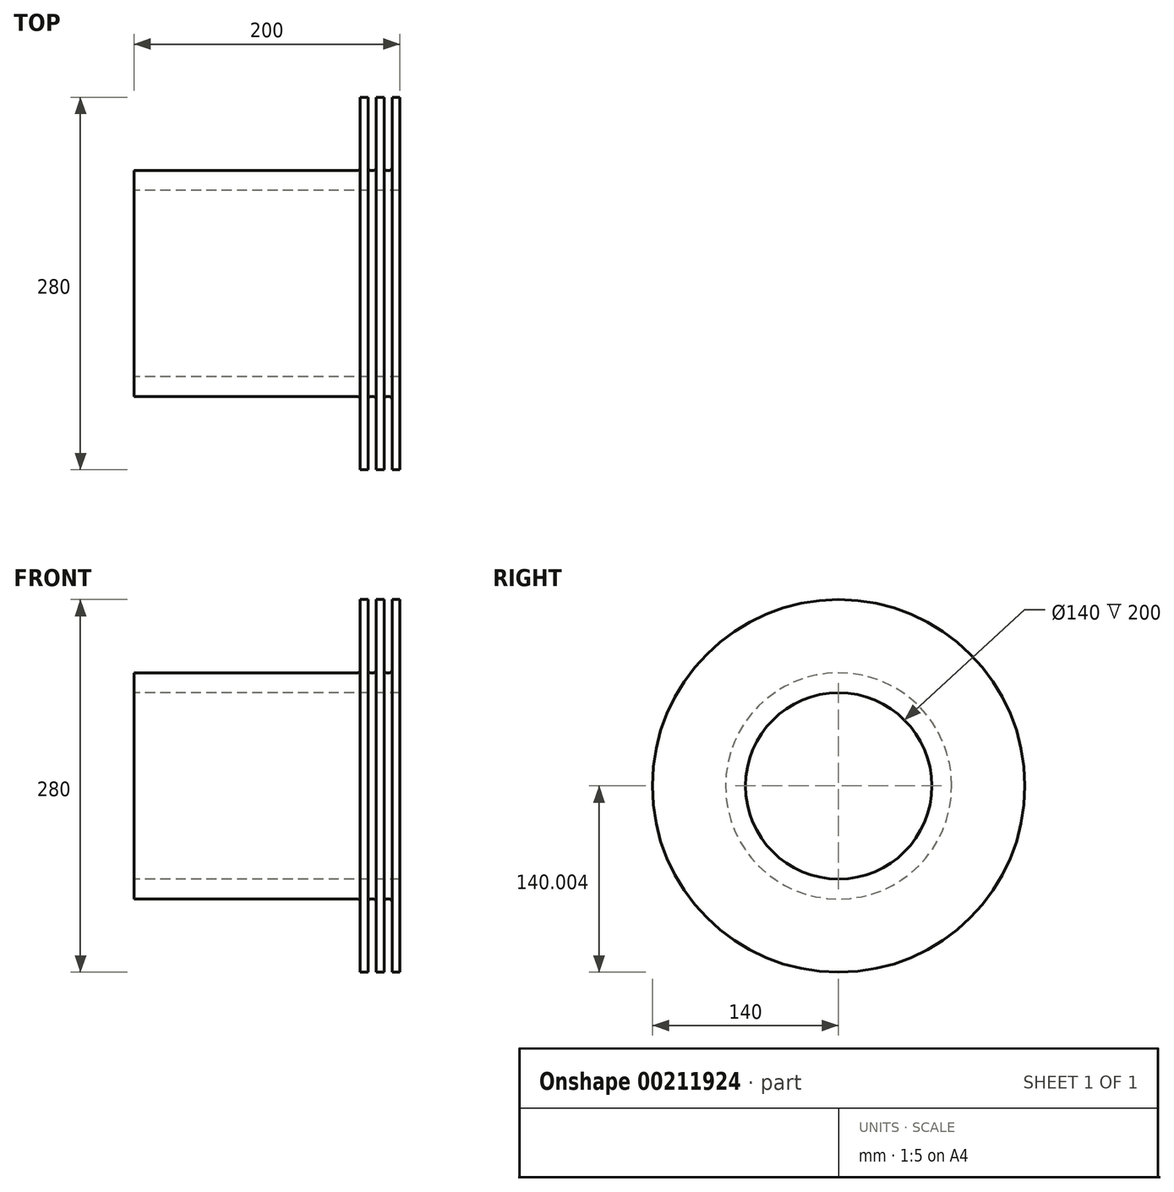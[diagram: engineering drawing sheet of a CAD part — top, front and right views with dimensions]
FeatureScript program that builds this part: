
annotation { "Feature Type Name" : "Feature", "Feature Type Description" : "" }
export const myFeature = defineFeature(function(context is Context, id is Id, definition is map)
    precondition{}
    {
        {
            var Q0;
            Q0=qCreatedBy(makeId("Front.planeOp"),FACE);
            var sketch = newSketch(context, id + "F0", { "sketchPlane" : qUnion([Q0])});
            skLineSegment(sketch, "E0", {"start": v(-102.97, -21.88) * mm, "end": v(97.03, -21.88) * mm});
            skLineSegment(sketch, "E1", {"start": v(97.03, -21.88) * mm, "end": v(97.03, 48.12) * mm});
            skLineSegment(sketch, "E2", {"start": v(97.03, 48.12) * mm, "end": v(91.03, 48.12) * mm});
            skLineSegment(sketch, "E3", {"start": v(-102.97, -6.88) * mm, "end": v(-102.97, -21.88) * mm});
            skLineSegment(sketch, "E4", {"start": v(91.03, 48.12) * mm, "end": v(91.03, -4.88) * mm});
            skLineSegment(sketch, "E5", {"start": v(77.03, -6.88) * mm, "end": v(75.03, -6.88) * mm});
            skArc(sketch, "E6.filletArc", {"start": v(89.03, -6.88) * mm, "mid": v(90.44, -6.29) * mm, "end": v(91.03, -4.88) * mm});
            skLineSegment(sketch, "E7", {"start": v(85.03, 48.12) * mm, "end": v(85.03, -4.88) * mm});
            skLineSegment(sketch, "E8", {"start": v(79.03, 48.12) * mm, "end": v(79.03, -4.88) * mm});
            skArc(sketch, "E9.filletArc", {"start": v(77.03, -6.88) * mm, "mid": v(78.44, -6.29) * mm, "end": v(79.03, -4.88) * mm});
            skLineSegment(sketch, "E10", {"start": v(87.03, -6.88) * mm, "end": v(89.03, -6.88) * mm});
            skPoint(sketch, "E11.visualSharp", {"position": v(85.03, -6.88) * mm});
            skArc(sketch, "E11.filletArc", {"start": v(85.03, -4.88) * mm, "mid": v(85.62, -6.29) * mm, "end": v(87.03, -6.88) * mm});
            skLineSegment(sketch, "E12.trimOffspring", {"start": v(85.03, 48.12) * mm, "end": v(79.03, 48.12) * mm});
            skPoint(sketch, "E13.orphan", {"position": v(-102.97, 48.12) * mm});
            skLineSegment(sketch, "E14", {"start": v(-118.37, -91.88) * mm, "end": v(109.53, -91.88) * mm});
            skLineSegment(sketch, "E15", {"start": v(73.03, -4.88) * mm, "end": v(73.03, 48.12) * mm});
            skLineSegment(sketch, "E16", {"start": v(73.03, 48.12) * mm, "end": v(67.03, 48.12) * mm});
            skLineSegment(sketch, "E17", {"start": v(67.03, 48.12) * mm, "end": v(67.03, -4.88) * mm});
            skLineSegment(sketch, "E18.trimOffspring", {"start": v(65.03, -6.88) * mm, "end": v(-102.97, -6.88) * mm});
            skPoint(sketch, "E19.visualSharp", {"position": v(73.03, -6.88) * mm});
            skArc(sketch, "E19.filletArc", {"start": v(73.03, -4.88) * mm, "mid": v(73.62, -6.29) * mm, "end": v(75.03, -6.88) * mm});
            skPoint(sketch, "E20.visualSharp", {"position": v(67.03, -6.88) * mm});
            skArc(sketch, "E20.filletArc", {"start": v(65.03, -6.88) * mm, "mid": v(66.44, -6.29) * mm, "end": v(67.03, -4.88) * mm});
            skSolve(sketch);
        }
        {
            var Q0;
            Q0=makeQuery(id+"F0.imprint","IMPRINT",FACE,{"disambiguationData":[TD([[makeQuery(id+"F0.imprint","IMPRINT",EDGE,{"derivedFrom":sQuery(id+"F0.wireOp",EDGE,"E0")}),1.0]])]});
            var Q1;
            Q1=sQuery(id+"F0.wireOp",EDGE,"E14");
            revolve(context, id + "F1", {"entities" : qUnion([Q0]), "axis" : qUnion([Q1]), "revolveType" : RevolveType.FULL});
        }
    });
